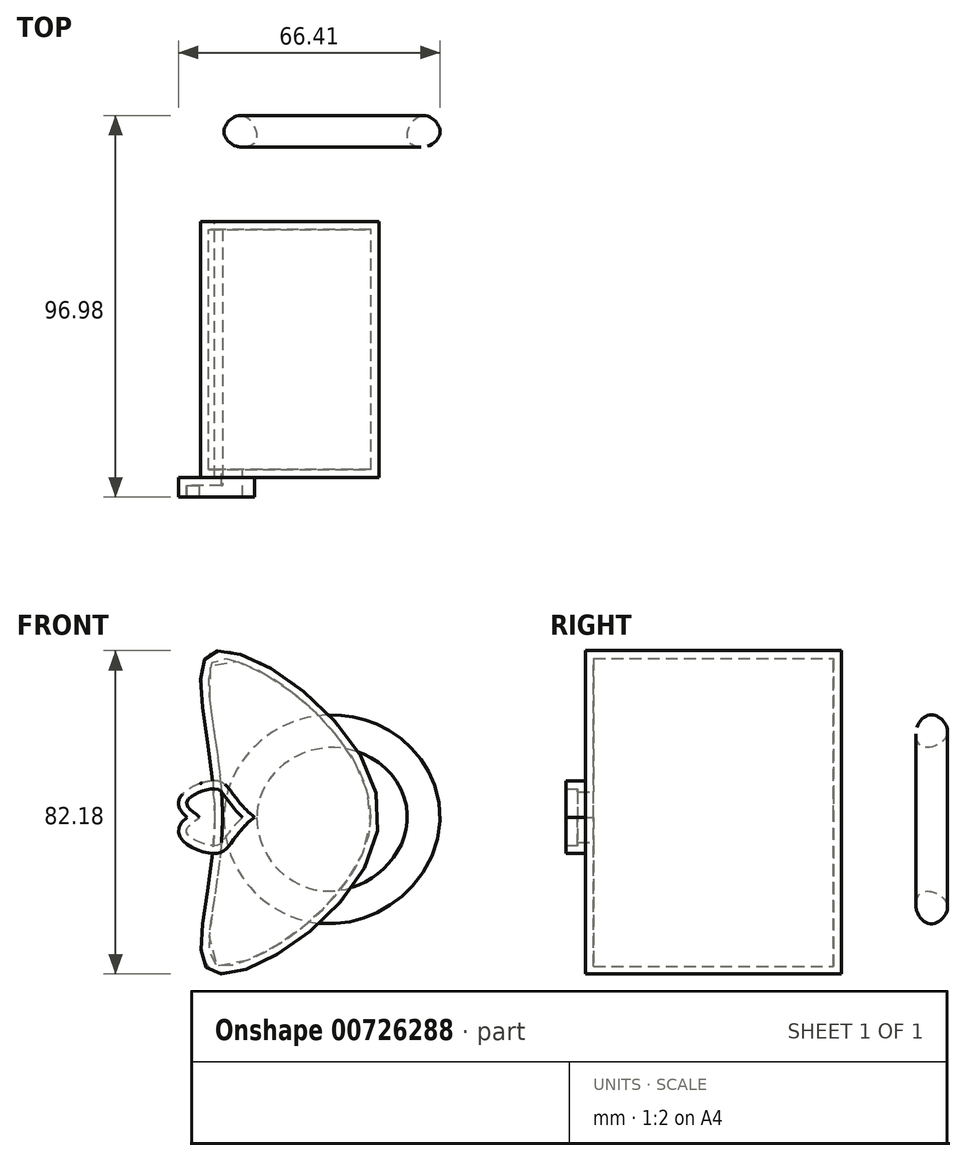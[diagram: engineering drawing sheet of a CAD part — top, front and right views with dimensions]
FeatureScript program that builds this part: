
annotation { "Feature Type Name" : "Feature", "Feature Type Description" : "" }
export const myFeature = defineFeature(function(context is Context, id is Id, definition is map)
    precondition{}
    {
        {
            var Q0;
            Q0=qCreatedBy(makeId("Front.planeOp"),FACE);
            var sketch = newSketch(context, id + "F0", { "sketchPlane" : qUnion([Q0])});
            skFitSpline(sketch, "E0", {"points": [v(0, 0) * mm, v(0, -39.62) * mm, v(41.74, 0) * mm, v(0, 42.1) * mm, v(0, 0) * mm]});
            skSolve(sketch);
        }
        {
            var Q0;
            Q0 = qSketchRegion(id + "F0", true);
            extrude(context, id + "F1", {"entities" : qUnion([Q0]), "endBound" : BoundingType.SYMMETRIC, "depth" : 65 * mm, "offsetDistance" : 25 * mm});
        }
        {
            var Q0;
            Q0=makeQuery(id+"F1.opExtrude","CAP_FACE",FACE,{"disambiguationData":[OSD([sQuery(id+"F0.wireOp",EDGE,"E0")])],"isStart":false});
            var sketch = newSketch(context, id + "F2", { "sketchPlane" : qUnion([Q0])});
            skFitSpline(sketch, "E1", {"points": [v(10.16, 0) * mm, v(-0.54, -9.22) * mm, v(-7, 0) * mm], "startDerivative": vector(-37.26, -29.33) * mm, "endDerivative": vector(38.9, 31.53) * mm});
            skFitSpline(sketch, "E2.MirrorCS", {"points": [v(10.16, 0) * mm, v(-0.54, 9.22) * mm, v(-7, 0) * mm], "startDerivative": vector(-37.26, 29.33) * mm, "endDerivative": vector(38.9, -31.53) * mm});
            skSolve(sketch);
        }
        {
            var Q0;
            Q0 = qSketchRegion(id + "F2", true);
            var Q1;
            {var subQ0=sQuery(id+"F2.wireOp",EDGE,"E2.MirrorCS");var subQ1=sQuery(id+"F2.wireOp",EDGE,"E1");var subQ2=makeQuery(id+"F2.imprint","INTERSECT",VERTEX,{"disambiguationData":[OD(0.0)],"derivedFrom":[subQ1,subQ0]});Q1=makeQuery(id+"F2.imprint","IMPRINT",FACE,{"disambiguationData":[TD([[makeQuery(id+"F2.imprint","IMPRINT",EDGE,{"disambiguationData":[TD([[subQ2,-1.0]])],"derivedFrom":subQ1}),-1.0]])]});}
            extrude(context, id + "F3", {"entities" : qUnion([Q0, Q1]), "operationType" : NewBodyOperationType.ADD, "depth" : 5 * mm, "offsetDistance" : 25 * mm});
        }
        {
            var Q0;
            Q0=makeQuery(id+"F3.opExtrude","CAP_FACE",FACE,{"disambiguationData":[OSD([sQuery(id+"F2.wireOp",EDGE,"E1"),sQuery(id+"F2.wireOp",EDGE,"E2.MirrorCS")])],"isStart":false});
            shell(context, id + "F4", {"entities" : qUnion([Q0]), "thickness" : 2 * mm});
        }
        {
            var Q0;
            Q0=qCreatedBy(makeId("Front.planeOp"),FACE);
            var sketch = newSketch(context, id + "F5", { "sketchPlane" : qUnion([Q0])});
            skFitSpline(sketch, "E3", {"points": [v(35.37, 0) * mm, v(29.89, 4.12) * mm, v(24.3, 0) * mm, v(28.9, -5.2) * mm, v(35.37, 0) * mm]});
            skSolve(sketch);
        }
        {
            var Q0;
            Q0=qCreatedBy(makeId("Top.planeOp"),FACE);
            var sketch = newSketch(context, id + "F6", { "sketchPlane" : qUnion([Q0])});
            skFitSpline(sketch, "E4", {"points": [v(5.59, 51.65) * mm, v(2.45, 55.9) * mm, v(7.25, 59.4) * mm, v(10.56, 53.31) * mm, v(5.59, 51.65) * mm]});
            skSolve(sketch);
        }
        {
            var Q0;
            Q0 = qSketchRegion(id + "F6", true);
            var Q1;
            Q1 = qConstructionFilter(qBodyType(qCreatedBy(id + "F5" ,EDGE), BodyType.WIRE), ConstructionObject.NO);
            sweep(context, id + "F7", {"profiles" : qUnion([Q0]), "path" : qUnion([Q1])});
        }
    });
